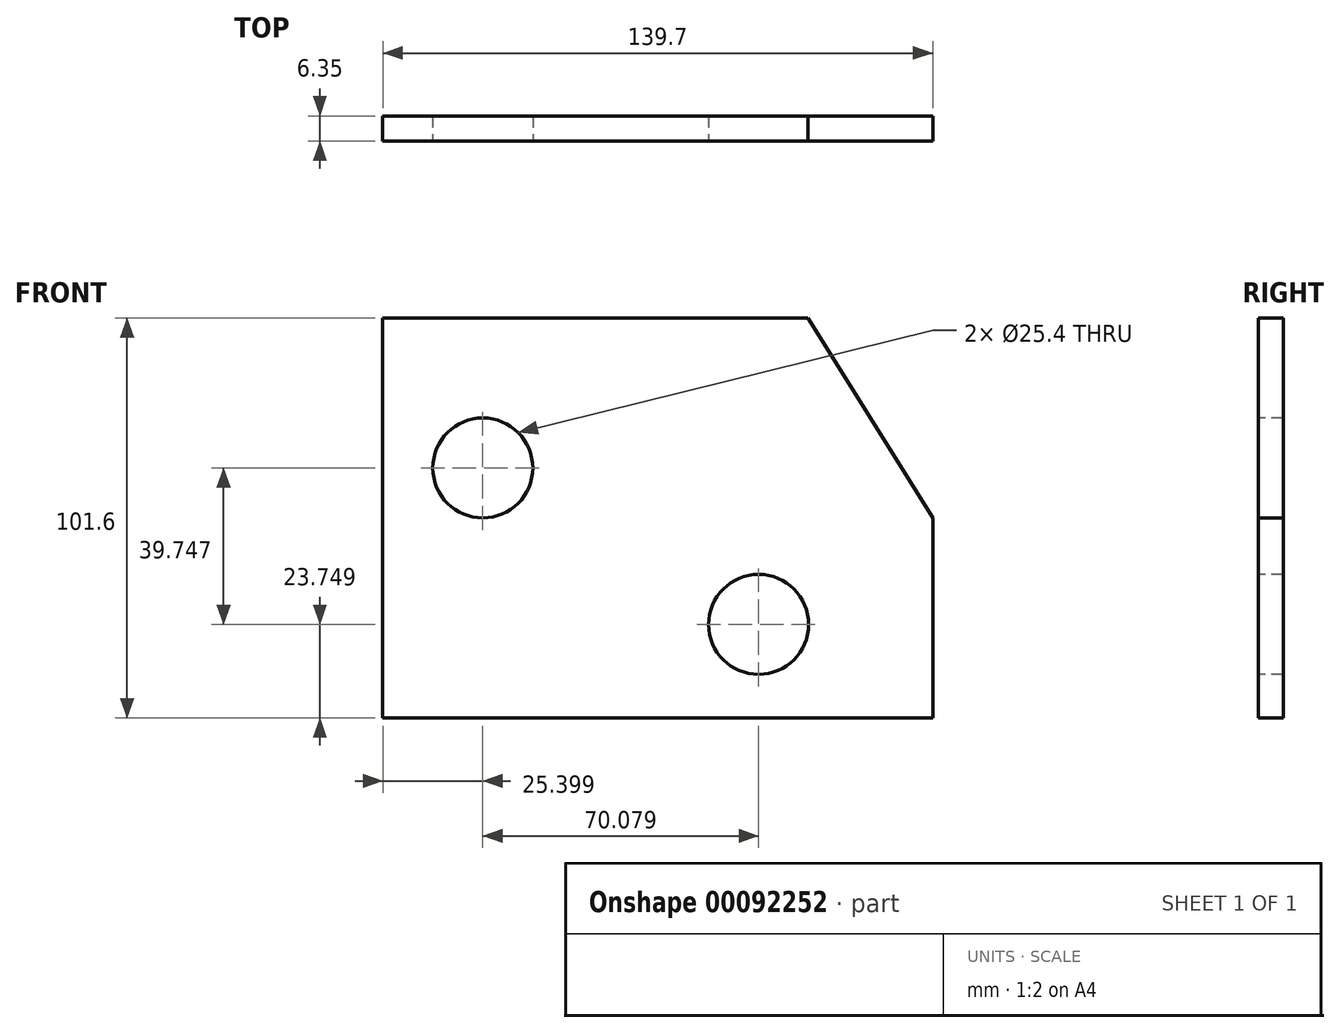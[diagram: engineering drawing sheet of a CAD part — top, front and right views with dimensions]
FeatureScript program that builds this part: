
annotation { "Feature Type Name" : "Feature", "Feature Type Description" : "" }
export const myFeature = defineFeature(function(context is Context, id is Id, definition is map)
    precondition{}
    {
        {
            var Q0;
            Q0=qCreatedBy(makeId("Front.planeOp"),FACE);
            var sketch = newSketch(context, id + "F0", { "sketchPlane" : qUnion([Q0])});
            skLineSegment(sketch, "E0", {"start": v(-53.95, 43.83) * mm, "end": v(-53.95, -57.77) * mm});
            skLineSegment(sketch, "E1", {"start": v(-53.95, -57.77) * mm, "end": v(85.75, -57.77) * mm});
            skLineSegment(sketch, "E2", {"start": v(85.75, -57.77) * mm, "end": v(85.75, -6.97) * mm});
            skLineSegment(sketch, "E3", {"start": v(85.75, -6.97) * mm, "end": v(54, 43.83) * mm});
            skLineSegment(sketch, "E4", {"start": v(54, 43.83) * mm, "end": v(-53.95, 43.83) * mm});
            skSolve(sketch);
        }
        {
            var Q0;
            Q0 = qSketchRegion(id + "F0", true);
            extrude(context, id + "F1", {"entities" : qUnion([Q0]), "depth" : 6.35 * mm});
        }
        {
            var Q0;
            Q0=makeQuery(id+"F1.opExtrude","CAP_FACE",FACE,{"disambiguationData":[OSD([sQuery(id+"F0.wireOp",EDGE,"E0"),sQuery(id+"F0.wireOp",EDGE,"E1"),sQuery(id+"F0.wireOp",EDGE,"E2"),sQuery(id+"F0.wireOp",EDGE,"E3"),sQuery(id+"F0.wireOp",EDGE,"E4")])],"isStart":false});
            var sketch = newSketch(context, id + "F2", { "sketchPlane" : qUnion([Q0])});
            skCircle(sketch, "E5", {"center": v(-28.55, 5.73) * mm, "radius": 12.7 * mm});
            skSolve(sketch);
        }
        {
            var Q0;
            Q0 = qSketchRegion(id + "F2", true);
            var Q1;
            Q1=makeQuery(id+"F1.opExtrude","SWEPT_BODY",BODY,{"disambiguationData":[OSD([sQuery(id+"F0.wireOp",EDGE,"E0"),sQuery(id+"F0.wireOp",EDGE,"E1"),sQuery(id+"F0.wireOp",EDGE,"E2"),sQuery(id+"F0.wireOp",EDGE,"E3"),sQuery(id+"F0.wireOp",EDGE,"E4")])]});
            extrude(context, id + "F3", {"entities" : qUnion([Q0]), "operationType" : NewBodyOperationType.REMOVE, "endBound" : BoundingType.THROUGH_ALL, "oppositeDirection" : true, "endBoundEntityBody" : qUnion([Q1]), "depth" : 25.4 * mm});
        }
        {
            var Q0;
            Q0=makeQuery(id+"F1.opExtrude","CAP_FACE",FACE,{"disambiguationData":[OSD([sQuery(id+"F0.wireOp",EDGE,"E0"),sQuery(id+"F0.wireOp",EDGE,"E1"),sQuery(id+"F0.wireOp",EDGE,"E2"),sQuery(id+"F0.wireOp",EDGE,"E3"),sQuery(id+"F0.wireOp",EDGE,"E4")])],"isStart":false});
            var sketch = newSketch(context, id + "F4", { "sketchPlane" : qUnion([Q0])});
            skPoint(sketch, "E6", {"position": v(41.53, -34.02) * mm});
            skSolve(sketch);
        }
        {
            var Q0;
            Q0=sQuery(id+"F4.wireOp",VERTEX,"E6");
            var Q1;
            Q1=makeQuery(id+"F1.opExtrude","SWEPT_BODY",BODY,{"disambiguationData":[OSD([sQuery(id+"F0.wireOp",EDGE,"E0"),sQuery(id+"F0.wireOp",EDGE,"E1"),sQuery(id+"F0.wireOp",EDGE,"E2"),sQuery(id+"F0.wireOp",EDGE,"E3"),sQuery(id+"F0.wireOp",EDGE,"E4")])]});
            hole(context, id + "F5", {"style" : HoleStyle.SIMPLE, "endStyle" : HoleEndStyle.THROUGH, "holeDiameter" : 25.4 * mm, "locations" : qUnion([Q0]), "scope" : qUnion([Q1]), "isTappedThrough" : true});
        }
    });
